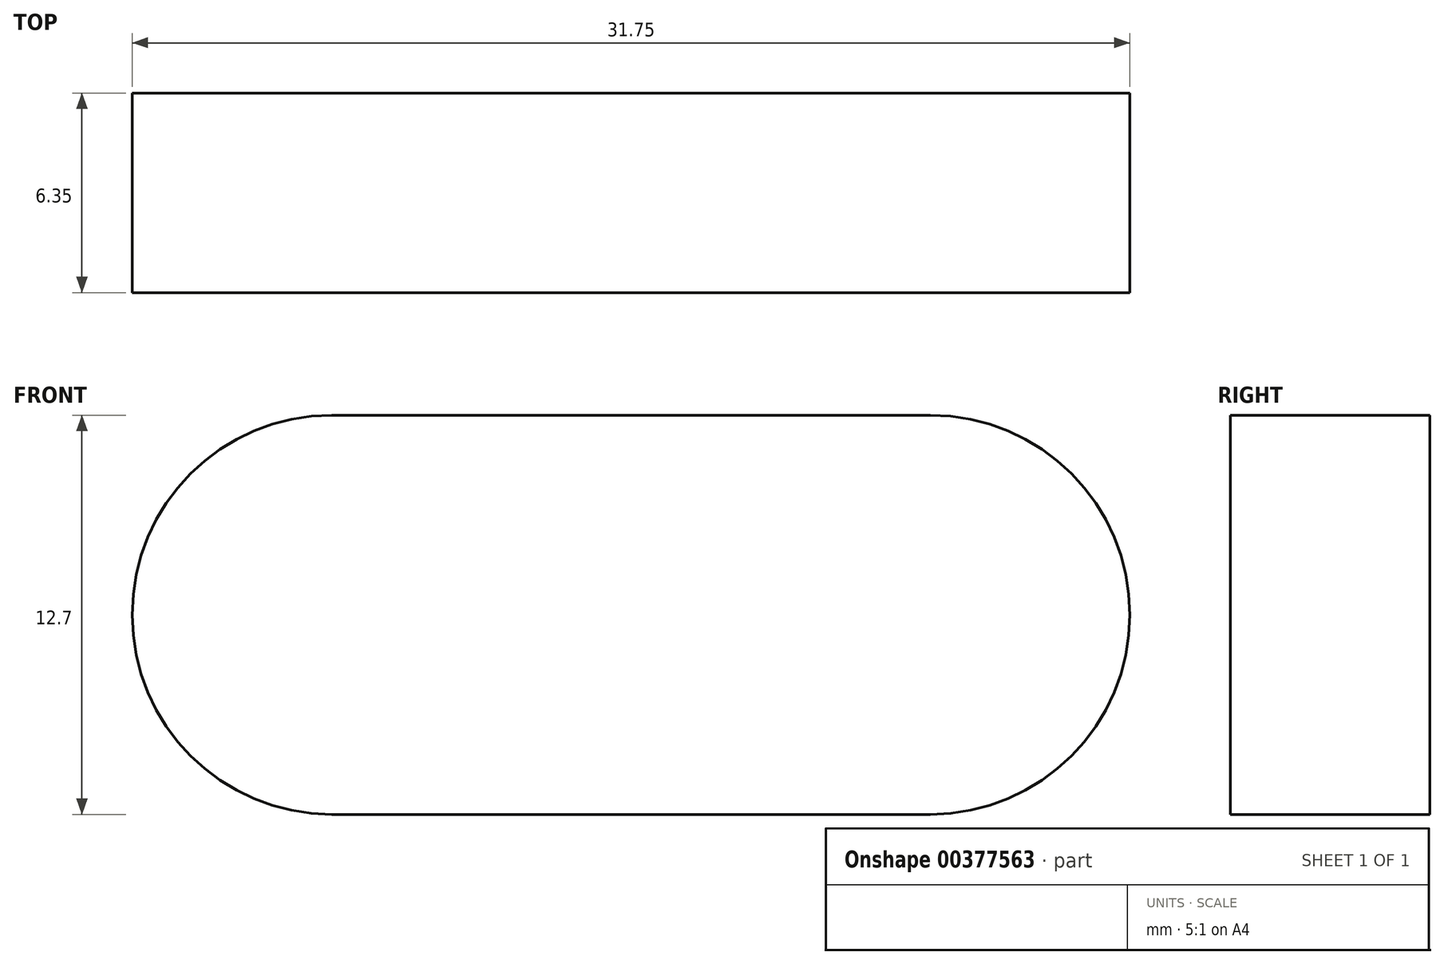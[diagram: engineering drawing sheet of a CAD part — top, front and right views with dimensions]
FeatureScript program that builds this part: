
annotation { "Feature Type Name" : "Feature", "Feature Type Description" : "" }
export const myFeature = defineFeature(function(context is Context, id is Id, definition is map)
    precondition{}
    {
        {
            var Q0;
            Q0=qCreatedBy(makeId("Front.planeOp"),FACE);
            var sketch = newSketch(context, id + "F0", { "sketchPlane" : qUnion([Q0])});
            skLineSegment(sketch, "E0.bottom", {"start": v(6.35, 0) * mm, "end": v(25.4, 0) * mm});
            skLineSegment(sketch, "E0.top", {"start": v(6.35, 12.7) * mm, "end": v(25.4, 12.7) * mm});
            skLineSegment(sketch, "E0.left", {"start": v(0, 6.35) * mm, "end": v(0, 6.35) * mm});
            skLineSegment(sketch, "E0.right", {"start": v(31.75, 6.35) * mm, "end": v(31.75, 6.35) * mm});
            skPoint(sketch, "E1.visualSharp", {"position": v(0, 12.7) * mm});
            skArc(sketch, "E1.filletArc", {"start": v(6.35, 12.7) * mm, "mid": v(1.86, 10.84) * mm, "end": v(0, 6.35) * mm});
            skPoint(sketch, "E2.visualSharp", {"position": v(0, 0) * mm});
            skArc(sketch, "E2.filletArc", {"start": v(0, 6.35) * mm, "mid": v(1.86, 1.86) * mm, "end": v(6.35, 0) * mm});
            skPoint(sketch, "E3.visualSharp", {"position": v(31.75, 12.7) * mm});
            skArc(sketch, "E3.filletArc", {"start": v(31.75, 6.35) * mm, "mid": v(29.9, 10.84) * mm, "end": v(25.4, 12.7) * mm});
            skPoint(sketch, "E4.visualSharp", {"position": v(31.75, 0) * mm});
            skArc(sketch, "E4.filletArc", {"start": v(25.4, 0) * mm, "mid": v(29.9, 1.86) * mm, "end": v(31.75, 6.35) * mm});
            skSolve(sketch);
        }
        {
            var Q0;
            Q0=qSketchRegion(id+"F0",true);
            extrude(context, id + "F1", {"entities" : qUnion([Q0]), "depth" : 6.35 * mm});
        }
    });
